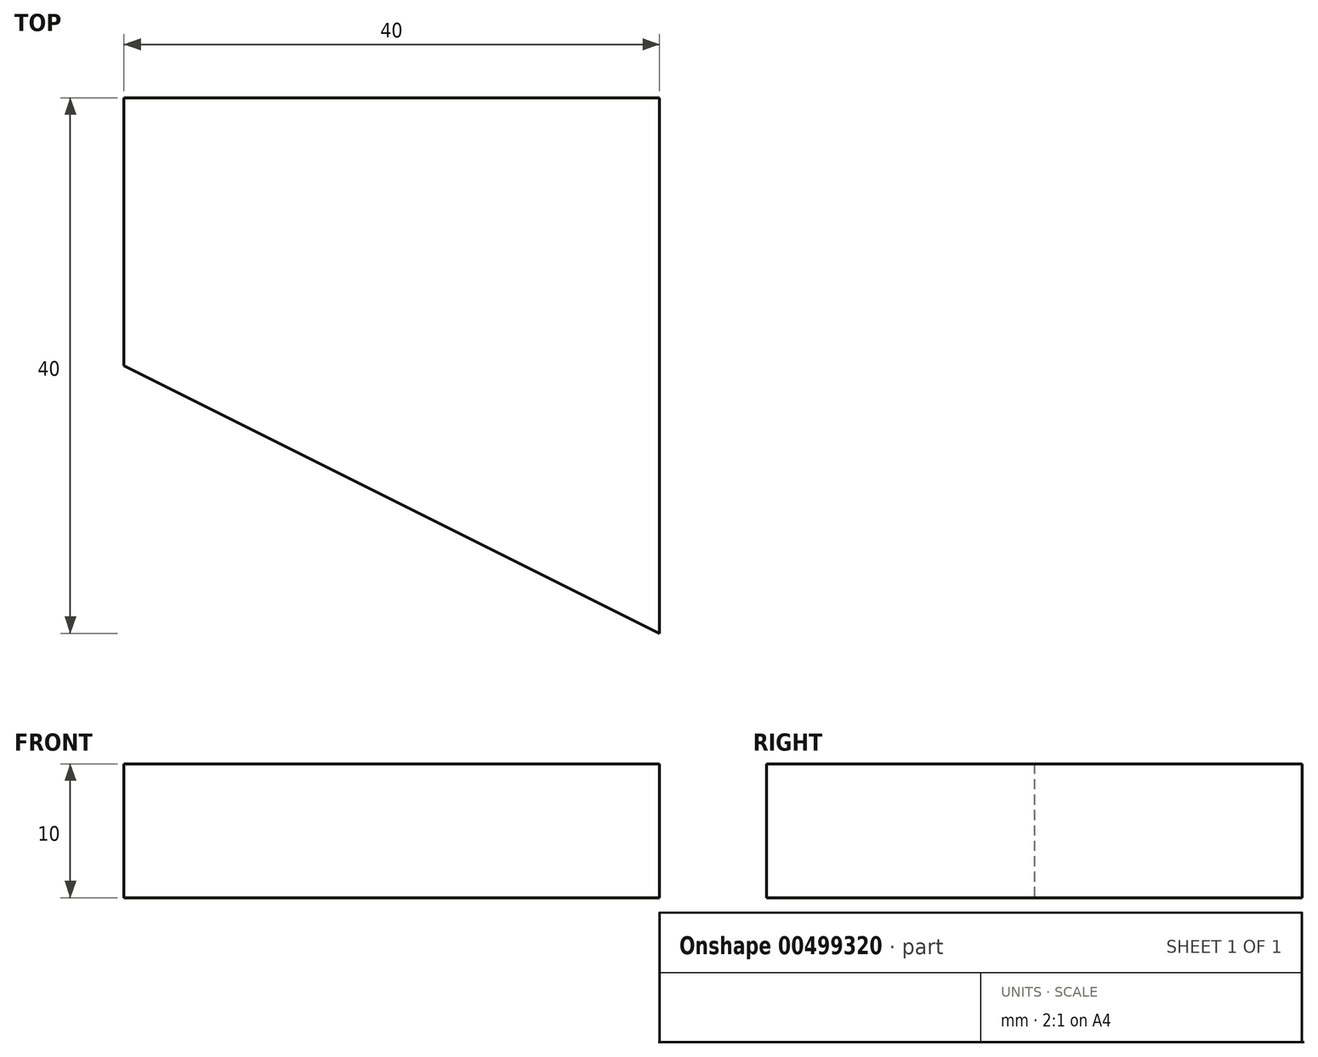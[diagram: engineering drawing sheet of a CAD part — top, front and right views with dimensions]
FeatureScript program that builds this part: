
annotation { "Feature Type Name" : "Feature", "Feature Type Description" : "" }
export const myFeature = defineFeature(function(context is Context, id is Id, definition is map)
    precondition{}
    {
        {
            var Q0;
            Q0=qCreatedBy(makeId("Top.planeOp"),FACE);
            var sketch = newSketch(context, id + "F0", { "sketchPlane" : qUnion([Q0])});
            skLineSegment(sketch, "E0", {"start": v(0, 0) * mm, "end": v(0, 20) * mm});
            skLineSegment(sketch, "E1", {"start": v(0, 20) * mm, "end": v(40, 20) * mm});
            skLineSegment(sketch, "E2", {"start": v(40, 20) * mm, "end": v(40, -20) * mm});
            skLineSegment(sketch, "E3", {"start": v(0, 0) * mm, "end": v(40, -20) * mm});
            skSolve(sketch);
        }
        {
            var Q0;
            Q0 = qSketchRegion(id + "F0", true);
            extrude(context, id + "F1", {"entities" : qUnion([Q0]), "depth" : 10 * mm});
        }
    });
